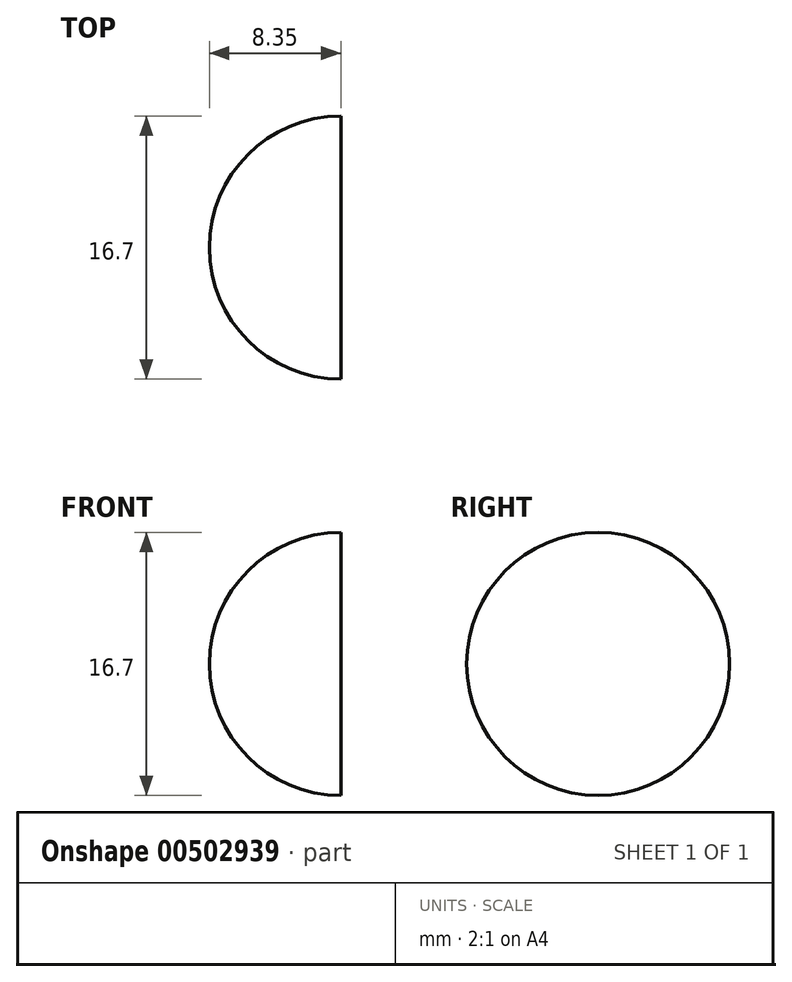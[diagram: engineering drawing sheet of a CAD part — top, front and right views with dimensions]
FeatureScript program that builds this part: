
annotation { "Feature Type Name" : "Feature", "Feature Type Description" : "" }
export const myFeature = defineFeature(function(context is Context, id is Id, definition is map)
    precondition{}
    {
        {
            var Q0;
            Q0=qCreatedBy(makeId("Front.planeOp"),FACE);
            var sketch = newSketch(context, id + "F0", { "sketchPlane" : qUnion([Q0])});
            skCircle(sketch, "E0", {"center": v(0, 0) * mm, "radius": 8.35 * mm});
            skLineSegment(sketch, "E1", {"start": v(0, 8.35) * mm, "end": v(0, -8.35) * mm});
            skSolve(sketch);
        }
        {
            var Q0;
            {var subQ0=sQuery(id+"F0.wireOp",EDGE,"E1");Q0=makeQuery(id+"F0.imprint","IMPRINT",FACE,{"disambiguationData":[TD([[makeQuery(id+"F0.imprint","IMPRINT",EDGE,{"derivedFrom":subQ0}),-1.0]])]});}
            var Q1;
            Q1=sQuery(id+"F0.wireOp",EDGE,"E1");
            revolve(context, id + "F1", {"entities" : qUnion([Q0]), "axis" : qUnion([Q1]), "revolveType" : RevolveType.SYMMETRIC, "angle" : 180 * degree});
        }
    });
